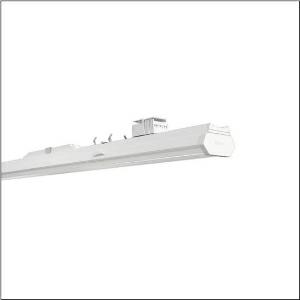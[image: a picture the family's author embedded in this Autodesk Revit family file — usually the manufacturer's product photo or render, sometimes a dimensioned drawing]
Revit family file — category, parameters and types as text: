
# Revit family: licross_r__21_protected_ho_52td12dn4axm_e376
name_source: partatom
category: Lighting Fixtures
units: mm (PartAtom-declared; Revit-internal decimal feet)

## family parameters
Cut with Voids When Loaded = No
Host = Face
Light Source = No
Part Type = Normal
Room Calculation Point = No
Round Connector Dimension = Use Diameter
Shared = No

## types (1)
- --- (1 x LED, 10000 lm, 56 W, 4000K)
    Apparent Load = 56 VA
    CIE Flux Codes = 70 91 97 98 100
    Color Rendering = 80
    Color Temperature = 4000K
    Default Elevation = 1800 mm
    Description = Licross® 21 Protected HO, luminaire insert, of sheet steel, galvanised, coil coated, white, length: 1.500mm, width: 90mm, height: 103mm, LED rated luminous flux: 10.000lm, light colour: 840, control gear: DALI 2, with plug, 5-pole, with phase selection, mains connection: 220..240V, AC, 50/60Hz, rated input power: 56W, halogen-free wiring, primary light control with lens, of plastic, primary optical cover: cover, of PMMA, light emission: direct distribution, primary light characteristic: symmetric, protection rating (complete): IP54, insulation class (complete): insulation class I (protective earthing), certification: CE, ENEC, VDE, UKCA, protection symbol: D if used in an environment with non-conductive dust loads with corresponding accessories, impact resistance: IK06, permissible ambient temperature for indoor applications: -25..+45°C, corresponds to IFS (International Featured Standards) requirements for safety and quality in the food industry, reducing of maximum allowable ambient temperature of 5°C with ceiling mounting, LABS conformity tested according to VDMA 24364:2018-05, packaging unit: 1 piece
    Height = 92 mm
    Lamp = 1 x LED
    Lamp Light Flux = 10000 lm
    Lamp Power = 56 W
    Lamp count = 1
    Length = 1500 mm
    Luminous efficacy = 179 lm/W
    Manufacturer = Siteco
    ModVariant = No
    Model = 52TD12DN4AXM
    Mounting Place = Ceiling
    Mounting Type = Pendant
    Number of Poles = 1
    OnlyDefault = Yes
    Power Factor = 1
    Product Name = Licross® 21 Protected HO
    Product group = luminaire insert
    ProductGroupID = 902
    Protection Class = Protection class I
    Protection Degree = IP 54
    RLX_Detail_Level = 1
    RLX_Emergency_Light_Flux = 0 lm
    RLX_Emergency_Type = 0
    RLX_Emergency_Type_DB = No
    RlxData = <blob elided: 24253 chars, md5=d966072d>
    Socket = socket
    Standby Power = 0 W
    System Light Flux = 10000 lm
    System Power = 56 W
    Type Comments = factory setting: luminous flux: 100 % | dim-lin: 254 | 321 mA
    Type Image = l_1256148.jpg
    URL = http://relux.com
    VarID = @adj_128970
    Voltage = 0 V
    Weight = 0.00 kg
    Width = 88 mm

## geometry (parser evidence)
native form markers: Blend x4, Sweep x13
no freeform markers — native parametric forms only
